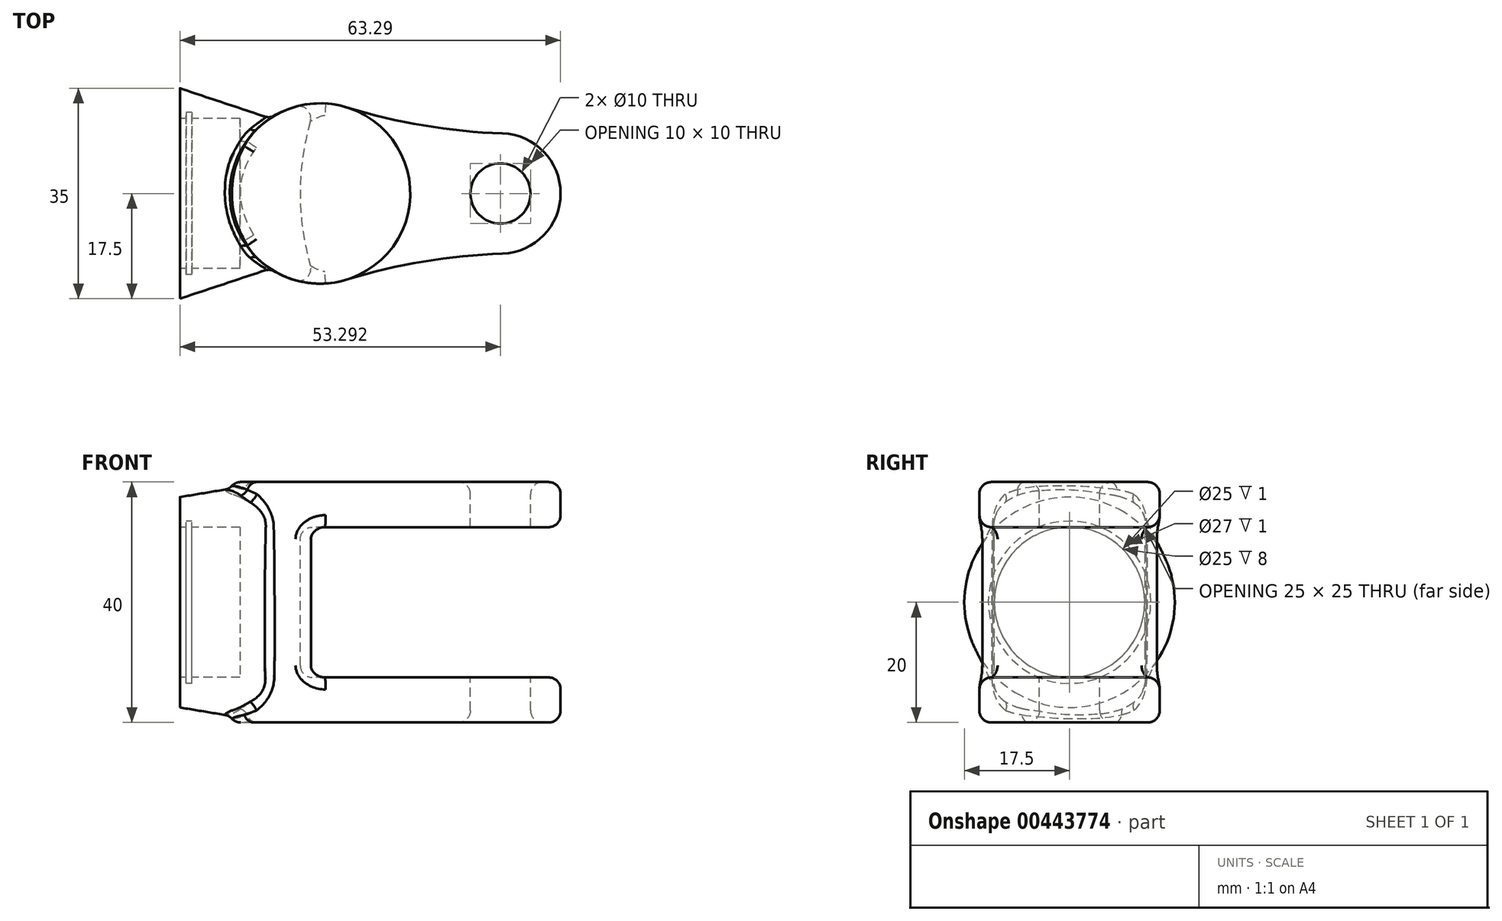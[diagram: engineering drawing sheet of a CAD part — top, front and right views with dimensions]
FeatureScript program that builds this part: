
annotation { "Feature Type Name" : "Feature", "Feature Type Description" : "" }
export const myFeature = defineFeature(function(context is Context, id is Id, definition is map)
    precondition{}
    {
        {
            var Q0;
            Q0=qCreatedBy(makeId("Right.planeOp"),FACE);
            var sketch = newSketch(context, id + "F0", { "sketchPlane" : qUnion([Q0])});
            skCircle(sketch, "E0", {"center": v(0, 0) * mm, "radius": 17.5 * mm});
            skSolve(sketch);
        }
        {
            var Q0;
            Q0=qCreatedBy(makeId("Right.planeOp"),FACE);
            cPlane(context, id + "F1", {"entities" : qUnion([Q0]), "cplaneType" : CPlaneType.OFFSET, "offset" : 15 * mm, "width" : 150 * mm, "height" : 150 * mm});
        }
        {
            var Q0;
            Q0=qCreatedBy(id+"F1.planeOp",FACE);
            var sketch = newSketch(context, id + "F2", { "sketchPlane" : qUnion([Q0])});
            skLineSegment(sketch, "E1.bottom", {"start": v(-5, 20) * mm, "end": v(5, 20) * mm});
            skLineSegment(sketch, "E1.top", {"start": v(-5, -20) * mm, "end": v(5, -20) * mm});
            skLineSegment(sketch, "E1.left", {"start": v(-12.5, 12.5) * mm, "end": v(-12.5, -12.5) * mm});
            skLineSegment(sketch, "E1.right", {"start": v(12.5, 12.5) * mm, "end": v(12.5, -12.5) * mm});
            skPoint(sketch, "E1.middle", {"position": v(0, 0) * mm});
            skPoint(sketch, "E2.visualSharp", {"position": v(-12.5, 20) * mm});
            skArc(sketch, "E2.filletArc", {"start": v(-5, 20) * mm, "mid": v(-10.3, 17.8) * mm, "end": v(-12.5, 12.5) * mm});
            skPoint(sketch, "E3.visualSharp", {"position": v(12.5, 20) * mm});
            skArc(sketch, "E3.filletArc", {"start": v(12.5, 12.5) * mm, "mid": v(10.3, 17.8) * mm, "end": v(5, 20) * mm});
            skPoint(sketch, "E4.visualSharp", {"position": v(12.5, -20) * mm});
            skArc(sketch, "E4.filletArc", {"start": v(5, -20) * mm, "mid": v(10.3, -17.8) * mm, "end": v(12.5, -12.5) * mm});
            skPoint(sketch, "E5.visualSharp", {"position": v(-12.5, -20) * mm});
            skArc(sketch, "E5.filletArc", {"start": v(-12.5, -12.5) * mm, "mid": v(-10.3, -17.8) * mm, "end": v(-5, -20) * mm});
            skSolve(sketch);
        }
        {
            var Q0;
            Q0 = qSketchRegion(id + "F0", true);
            var Q1;
            Q1 = qSketchRegion(id + "F2", true);
            loft(context, id + "F3", {"sheetProfilesArray" : [{ "sheetProfileEntities" : qUnion([Q0]) }, { "sheetProfileEntities" : qUnion([Q1]) }]});
        }
        {
            var Q0;
            Q0=qCreatedBy(makeId("Top.planeOp"),FACE);
            var sketch = newSketch(context, id + "F4", { "sketchPlane" : qUnion([Q0])});
            skArc(sketch, "E6", {"start": v(27.7, 14.34) * mm, "mid": v(8.3, 0) * mm, "end": v(27.7, -14.34) * mm});
            skArc(sketch, "E7", {"start": v(53.63, -10) * mm, "mid": v(63.3, 0) * mm, "end": v(53.63, 10) * mm});
            skArc(sketch, "E8", {"start": v(53.63, -10) * mm, "mid": v(40.52, -11.31) * mm, "end": v(27.7, -14.34) * mm});
            skArc(sketch, "E9", {"start": v(27.7, 14.34) * mm, "mid": v(40.52, 11.31) * mm, "end": v(53.63, 10) * mm});
            skSolve(sketch);
        }
        {
            var Q0;
            Q0 = qSketchRegion(id + "F4", true);
            extrude(context, id + "F5", {"entities" : qUnion([Q0]), "operationType" : NewBodyOperationType.ADD, "endBound" : BoundingType.SYMMETRIC, "depth" : 40 * mm});
        }
        {
            var Q0;
            Q0=qCreatedBy(makeId("Front.planeOp"),FACE);
            var sketch = newSketch(context, id + "F6", { "sketchPlane" : qUnion([Q0])});
            skLineSegment(sketch, "E10.bottom", {"start": v(20, -12.5) * mm, "end": v(63.3, -12.5) * mm});
            skLineSegment(sketch, "E10.top", {"start": v(20, 12.5) * mm, "end": v(63.3, 12.5) * mm});
            skLineSegment(sketch, "E10.left", {"start": v(20, -12.5) * mm, "end": v(20, 12.5) * mm});
            skLineSegment(sketch, "E10.right", {"start": v(63.3, -12.5) * mm, "end": v(63.3, 12.5) * mm});
            skSolve(sketch);
        }
        {
            var Q0;
            Q0 = qSketchRegion(id + "F6", true);
            var Q1;
            Q1=sQuery(id+"F6.wireOp",EDGE,"E10.right");
            revolve(context, id + "F7", {"operationType" : NewBodyOperationType.REMOVE, "entities" : qUnion([Q0]), "axis" : qUnion([Q1]), "revolveType" : RevolveType.FULL, "oppositeDirection" : true});
        }
        {
            var Q0;
            Q0=makeQuery(id+"F3.opLoft","CAP_FACE",FACE,{"disambiguationData":[OSD([makeQuery(id+"F0.imprint","IMPRINT",FACE,{"disambiguationData":[TD([[makeQuery(id+"F0.imprint","IMPRINT",EDGE,{"derivedFrom":sQuery(id+"F0.wireOp",EDGE,"E0")}),1.0]])]})])],"isStart":true});
            var sketch = newSketch(context, id + "F8", { "sketchPlane" : qUnion([Q0])});
            skCircle(sketch, "E11", {"center": v(0, 0) * mm, "radius": 12.5 * mm});
            skSolve(sketch);
        }
        {
            var Q0;
            Q0 = qSketchRegion(id + "F8", true);
            extrude(context, id + "F9", {"entities" : qUnion([Q0]), "operationType" : NewBodyOperationType.REMOVE, "oppositeDirection" : true, "depth" : 10 * mm});
        }
        {
            var Q0;
            Q0=qCreatedBy(makeId("Right.planeOp"),FACE);
            cPlane(context, id + "F10", {"entities" : qUnion([Q0]), "cplaneType" : CPlaneType.OFFSET, "offset" : 1 * mm, "width" : 150 * mm, "height" : 150 * mm});
        }
        {
            var Q0;
            Q0=qCreatedBy(id+"F10.planeOp",FACE);
            var sketch = newSketch(context, id + "F11", { "sketchPlane" : qUnion([Q0])});
            skCircle(sketch, "E12.0", {"center": v(0, 0) * mm, "radius": 13.5 * mm});
            skSolve(sketch);
        }
        {
            var Q0;
            Q0 = qSketchRegion(id + "F11", true);
            extrude(context, id + "F12", {"entities" : qUnion([Q0]), "operationType" : NewBodyOperationType.REMOVE, "depth" : 1 * mm});
        }
        {
            var Q0;
            Q0=makeQuery(id+"F5.opExtrude","CAP_FACE",FACE,{"disambiguationData":[OSD([sQuery(id+"F4.wireOp",EDGE,"E6"),sQuery(id+"F4.wireOp",EDGE,"E7"),sQuery(id+"F4.wireOp",EDGE,"E8"),sQuery(id+"F4.wireOp",EDGE,"E9")])],"isStart":false});
            var sketch = newSketch(context, id + "F13", { "sketchPlane" : qUnion([Q0])});
            skCircle(sketch, "E13", {"center": v(53.3, 0) * mm, "radius": 5 * mm});
            skSolve(sketch);
        }
        {
            var Q0;
            Q0 = qSketchRegion(id + "F13", true);
            extrude(context, id + "F14", {"entities" : qUnion([Q0]), "operationType" : NewBodyOperationType.REMOVE, "endBound" : BoundingType.THROUGH_ALL, "oppositeDirection" : true, "depth" : 25 * mm});
        }
        {
            var Q0;
            Q0=makeQuery(id+"F7.boolean.opBoolean","COPY",EDGE,{"derivedFrom":makeQuery(id+"F7.opRevolve","SWEPT_EDGE",EDGE,{"disambiguationData":[OSD([sQuery(id+"F6.wireOp",EDGE,"E10.top"),sQuery(id+"F6.wireOp",EDGE,"E10.left")])]})});
            var Q1;
            Q1=makeQuery(id+"F7.boolean.opBoolean","COPY",EDGE,{"derivedFrom":makeQuery(id+"F7.opRevolve","SWEPT_EDGE",EDGE,{"disambiguationData":[OSD([sQuery(id+"F6.wireOp",EDGE,"E10.bottom"),sQuery(id+"F6.wireOp",EDGE,"E10.left")])]})});
            fillet(context, id + "F15", {"entities" : qUnion([Q0, Q1]), "radius" : 2 * mm, "tangentPropagation" : true, "allowEdgeOverflow" : false});
        }
        {
            var Q0;
            Q0=makeQuery(id+"F5.opExtrude","CAP_FACE",FACE,{"disambiguationData":[OSD([sQuery(id+"F4.wireOp",EDGE,"E6"),sQuery(id+"F4.wireOp",EDGE,"E7"),sQuery(id+"F4.wireOp",EDGE,"E8"),sQuery(id+"F4.wireOp",EDGE,"E9")])],"isStart":false});
            var Q1;
            Q1=makeQuery(id+"F5.opExtrude","CAP_FACE",FACE,{"disambiguationData":[OSD([sQuery(id+"F4.wireOp",EDGE,"E6"),sQuery(id+"F4.wireOp",EDGE,"E7"),sQuery(id+"F4.wireOp",EDGE,"E8"),sQuery(id+"F4.wireOp",EDGE,"E9")])],"isStart":true});
            var Q2;
            Q2=makeQuery(id+"F7.boolean.opBoolean","INTERSECT",EDGE,{"disambiguationData":[OD(1.0)],"derivedFrom":[makeQuery(id+"F5.opExtrude","SWEPT_FACE",FACE,{"disambiguationData":[OSD([sQuery(id+"F4.wireOp",EDGE,"E6")])]}),makeQuery(id+"F7.opRevolve","SWEPT_FACE",FACE,{"disambiguationData":[OSD([sQuery(id+"F6.wireOp",EDGE,"E10.left")])]})]});
            var Q3;
            Q3=makeQuery(id+"F14.boolean.opBoolean","COPY",EDGE,{"derivedFrom":makeQuery(id+"F14.opExtrude","CAP_EDGE",EDGE,{"disambiguationData":[OSD([sQuery(id+"F13.wireOp",EDGE,"E13")])],"isStart":true})});
            fillet(context, id + "F16", {"entities" : qUnion([Q0, Q1, Q2, Q3]), "radius" : 2 * mm, "tangentPropagation" : true, "allowEdgeOverflow" : false});
        }
        {
            var Q0;
            Q0=makeQuery(id+"F16.opFillet","BLEND_EDGE",EDGE,{"blendedFrom":[makeQuery(id+"F5.opExtrude","CAP_EDGE",EDGE,{"disambiguationData":[OSD([sQuery(id+"F4.wireOp",EDGE,"E6")])],"isStart":false}),makeQuery(id+"F3.opLoft","SWEPT_FACE",FACE,{"disambiguationData":[OSD([sQuery(id+"F0.wireOp",EDGE,"E0"),sQuery(id+"F2.wireOp",EDGE,"E1.bottom"),sQuery(id+"F2.wireOp",EDGE,"E1.left"),sQuery(id+"F2.wireOp",EDGE,"E2.filletArc")])]})],"blendedInto":[makeQuery(id+"F3.opLoft","SWEPT_FACE",FACE,{"disambiguationData":[OSD([sQuery(id+"F0.wireOp",EDGE,"E0"),sQuery(id+"F2.wireOp",EDGE,"E1.bottom"),sQuery(id+"F2.wireOp",EDGE,"E1.left"),sQuery(id+"F2.wireOp",EDGE,"E2.filletArc")])]})]});
            fillet(context, id + "F17", {"entities" : qUnion([Q0]), "radius" : 2 * mm, "tangentPropagation" : true, "allowEdgeOverflow" : false});
        }
    });
